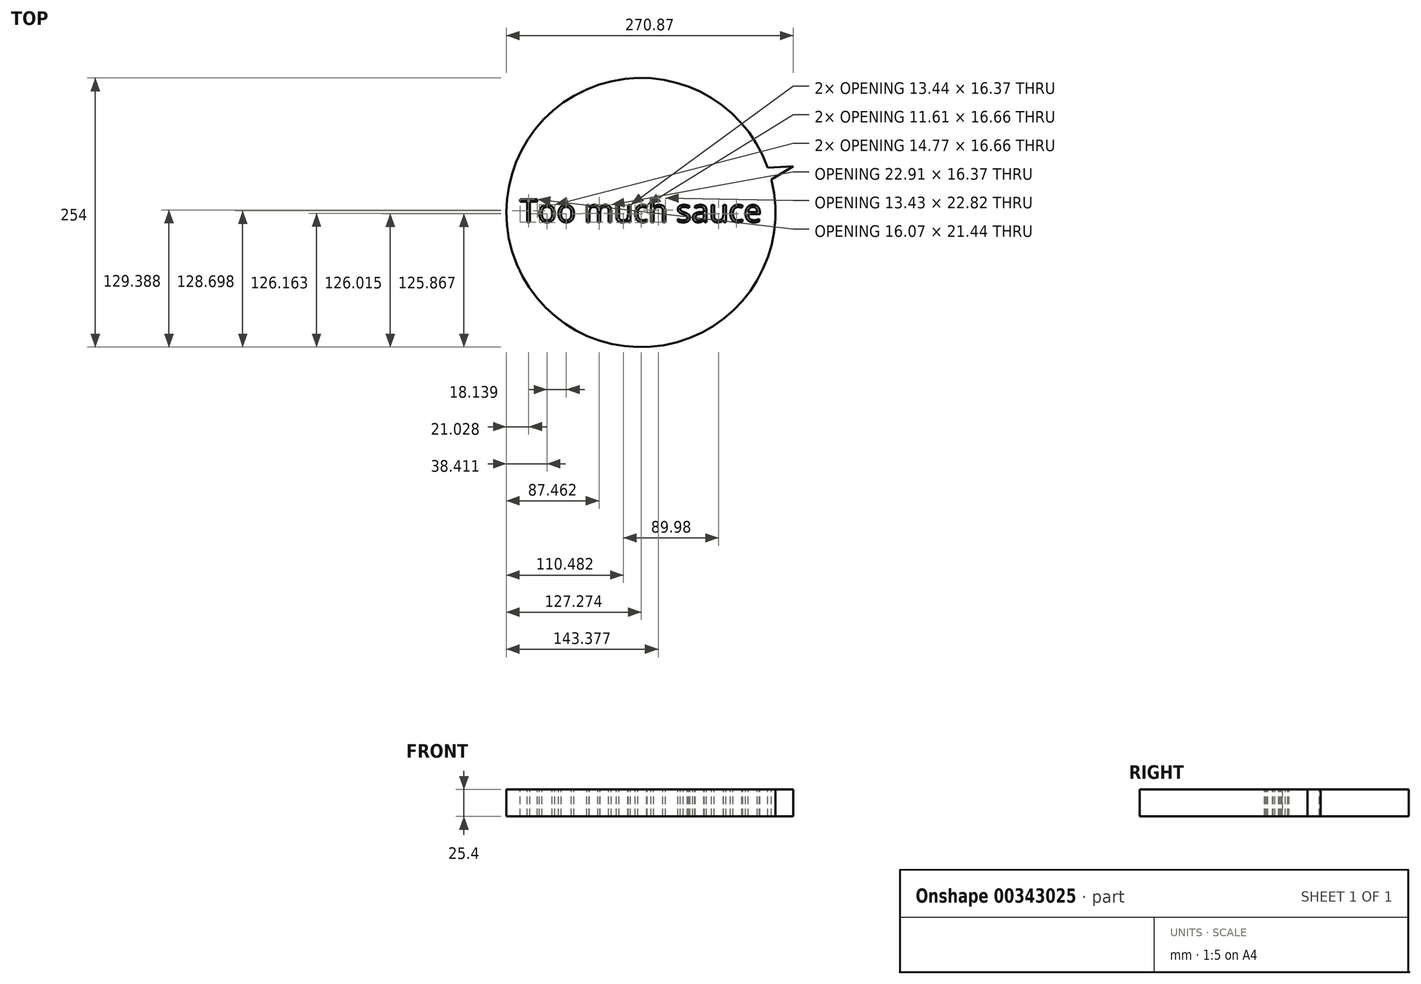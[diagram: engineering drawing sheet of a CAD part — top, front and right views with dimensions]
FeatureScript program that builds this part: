
annotation { "Feature Type Name" : "Feature", "Feature Type Description" : "" }
export const myFeature = defineFeature(function(context is Context, id is Id, definition is map)
    precondition{}
    {
        {
            var Q0;
            Q0=qCreatedBy(makeId("Top.planeOp"),FACE);
            var sketch = newSketch(context, id + "F0", { "sketchPlane" : qUnion([Q0])});
            skCircle(sketch, "E0", {"center": v(0, 0) * mm, "radius": 127 * mm});
            skSolve(sketch);
        }
        {
            var Q0;
            Q0 = qSketchRegion(id + "F0", true);
            extrude(context, id + "F1", {"entities" : qUnion([Q0]), "endBound" : BoundingType.SYMMETRIC, "depth" : 25.4 * mm});
        }
        {
            var Q0;
            Q0=makeQuery(id+"F1.opExtrude","CAP_FACE",FACE,{"disambiguationData":[OSD([sQuery(id+"F0.wireOp",EDGE,"E0")])],"isStart":false});
            var sketch = newSketch(context, id + "F2", { "sketchPlane" : qUnion([Q0])});
            skLineSegment(sketch, "E1", {"start": v(0, 0) * mm, "end": v(123.1, 31.24) * mm, "construction": true});
            skLineSegment(sketch, "E2", {"start": v(0, 0) * mm, "end": v(119.75, 42.3) * mm, "construction": true});
            skLineSegment(sketch, "E3", {"start": v(119.75, 42.3) * mm, "end": v(123.1, 31.24) * mm});
            skLineSegment(sketch, "E4", {"start": v(119.75, 42.3) * mm, "end": v(143.87, 43.57) * mm});
            skLineSegment(sketch, "E5", {"start": v(143.87, 43.57) * mm, "end": v(123.1, 31.24) * mm});
            skSolve(sketch);
        }
        {
            var Q0;
            Q0 = qSketchRegion(id + "F2", true);
            extrude(context, id + "F3", {"entities" : qUnion([Q0]), "operationType" : NewBodyOperationType.ADD, "oppositeDirection" : true, "depth" : 25.4 * mm});
        }
        {
            var Q0;
            {var subQ0=sQuery(id+"F2.wireOp",EDGE,"E5");var subQ1=sQuery(id+"F2.wireOp",EDGE,"E4");var subQ2=sQuery(id+"F2.wireOp",EDGE,"E3");Q0=makeQuery(id+"FsgY7ZD5xx5v8C2_1.68.F3.boolean.opBoolean","MERGE",FACE,{"derivedFrom":[makeQuery(id+"FsgY7ZD5xx5v8C2_1.67.F3.boolean.opBoolean","MERGE",FACE,{"derivedFrom":[makeQuery(id+"FsgY7ZD5xx5v8C2_1.66.F3.boolean.opBoolean","MERGE",FACE,{"derivedFrom":[makeQuery(id+"FsgY7ZD5xx5v8C2_1.65.F3.boolean.opBoolean","MERGE",FACE,{"derivedFrom":[makeQuery(id+"FsgY7ZD5xx5v8C2_1.64.F3.boolean.opBoolean","MERGE",FACE,{"derivedFrom":[makeQuery(id+"FsgY7ZD5xx5v8C2_1.63.F3.boolean.opBoolean","MERGE",FACE,{"derivedFrom":[makeQuery(id+"FsgY7ZD5xx5v8C2_1.62.F3.boolean.opBoolean","MERGE",FACE,{"derivedFrom":[makeQuery(id+"FsgY7ZD5xx5v8C2_1.61.F3.boolean.opBoolean","MERGE",FACE,{"derivedFrom":[makeQuery(id+"FsgY7ZD5xx5v8C2_1.60.F3.boolean.opBoolean","MERGE",FACE,{"derivedFrom":[makeQuery(id+"FsgY7ZD5xx5v8C2_1.59.F3.boolean.opBoolean","MERGE",FACE,{"derivedFrom":[makeQuery(id+"FsgY7ZD5xx5v8C2_1.58.F3.boolean.opBoolean","MERGE",FACE,{"derivedFrom":[makeQuery(id+"FsgY7ZD5xx5v8C2_1.57.F3.boolean.opBoolean","MERGE",FACE,{"derivedFrom":[makeQuery(id+"FsgY7ZD5xx5v8C2_1.56.F3.boolean.opBoolean","MERGE",FACE,{"derivedFrom":[makeQuery(id+"FsgY7ZD5xx5v8C2_1.55.F3.boolean.opBoolean","MERGE",FACE,{"derivedFrom":[makeQuery(id+"FsgY7ZD5xx5v8C2_1.54.F3.boolean.opBoolean","MERGE",FACE,{"derivedFrom":[makeQuery(id+"FsgY7ZD5xx5v8C2_1.53.F3.boolean.opBoolean","MERGE",FACE,{"derivedFrom":[makeQuery(id+"FsgY7ZD5xx5v8C2_1.52.F3.boolean.opBoolean","MERGE",FACE,{"derivedFrom":[makeQuery(id+"FsgY7ZD5xx5v8C2_1.51.F3.boolean.opBoolean","MERGE",FACE,{"derivedFrom":[makeQuery(id+"FsgY7ZD5xx5v8C2_1.50.F3.boolean.opBoolean","MERGE",FACE,{"derivedFrom":[makeQuery(id+"FsgY7ZD5xx5v8C2_1.49.F3.boolean.opBoolean","MERGE",FACE,{"derivedFrom":[makeQuery(id+"FsgY7ZD5xx5v8C2_1.48.F3.boolean.opBoolean","MERGE",FACE,{"derivedFrom":[makeQuery(id+"FsgY7ZD5xx5v8C2_1.47.F3.boolean.opBoolean","MERGE",FACE,{"derivedFrom":[makeQuery(id+"FsgY7ZD5xx5v8C2_1.46.F3.boolean.opBoolean","MERGE",FACE,{"derivedFrom":[makeQuery(id+"FsgY7ZD5xx5v8C2_1.45.F3.boolean.opBoolean","MERGE",FACE,{"derivedFrom":[makeQuery(id+"FsgY7ZD5xx5v8C2_1.44.F3.boolean.opBoolean","MERGE",FACE,{"derivedFrom":[makeQuery(id+"FsgY7ZD5xx5v8C2_1.43.F3.boolean.opBoolean","MERGE",FACE,{"derivedFrom":[makeQuery(id+"FsgY7ZD5xx5v8C2_1.42.F3.boolean.opBoolean","MERGE",FACE,{"derivedFrom":[makeQuery(id+"FsgY7ZD5xx5v8C2_1.41.F3.boolean.opBoolean","MERGE",FACE,{"derivedFrom":[makeQuery(id+"FsgY7ZD5xx5v8C2_1.40.F3.boolean.opBoolean","MERGE",FACE,{"derivedFrom":[makeQuery(id+"FsgY7ZD5xx5v8C2_1.39.F3.boolean.opBoolean","MERGE",FACE,{"derivedFrom":[makeQuery(id+"FsgY7ZD5xx5v8C2_1.38.F3.boolean.opBoolean","MERGE",FACE,{"derivedFrom":[makeQuery(id+"FsgY7ZD5xx5v8C2_1.37.F3.boolean.opBoolean","MERGE",FACE,{"derivedFrom":[makeQuery(id+"FsgY7ZD5xx5v8C2_1.36.F3.boolean.opBoolean","MERGE",FACE,{"derivedFrom":[makeQuery(id+"FsgY7ZD5xx5v8C2_1.35.F3.boolean.opBoolean","MERGE",FACE,{"derivedFrom":[makeQuery(id+"FsgY7ZD5xx5v8C2_1.34.F3.boolean.opBoolean","MERGE",FACE,{"derivedFrom":[makeQuery(id+"FsgY7ZD5xx5v8C2_1.33.F3.boolean.opBoolean","MERGE",FACE,{"derivedFrom":[makeQuery(id+"FsgY7ZD5xx5v8C2_1.32.F3.boolean.opBoolean","MERGE",FACE,{"derivedFrom":[makeQuery(id+"FsgY7ZD5xx5v8C2_1.31.F3.boolean.opBoolean","MERGE",FACE,{"derivedFrom":[makeQuery(id+"FsgY7ZD5xx5v8C2_1.30.F3.boolean.opBoolean","MERGE",FACE,{"derivedFrom":[makeQuery(id+"FsgY7ZD5xx5v8C2_1.29.F3.boolean.opBoolean","MERGE",FACE,{"derivedFrom":[makeQuery(id+"FsgY7ZD5xx5v8C2_1.28.F3.boolean.opBoolean","MERGE",FACE,{"derivedFrom":[makeQuery(id+"FsgY7ZD5xx5v8C2_1.27.F3.boolean.opBoolean","MERGE",FACE,{"derivedFrom":[makeQuery(id+"FsgY7ZD5xx5v8C2_1.26.F3.boolean.opBoolean","MERGE",FACE,{"derivedFrom":[makeQuery(id+"FsgY7ZD5xx5v8C2_1.25.F3.boolean.opBoolean","MERGE",FACE,{"derivedFrom":[makeQuery(id+"FsgY7ZD5xx5v8C2_1.24.F3.boolean.opBoolean","MERGE",FACE,{"derivedFrom":[makeQuery(id+"FsgY7ZD5xx5v8C2_1.23.F3.boolean.opBoolean","MERGE",FACE,{"derivedFrom":[makeQuery(id+"FsgY7ZD5xx5v8C2_1.22.F3.boolean.opBoolean","MERGE",FACE,{"derivedFrom":[makeQuery(id+"FsgY7ZD5xx5v8C2_1.21.F3.boolean.opBoolean","MERGE",FACE,{"derivedFrom":[makeQuery(id+"FsgY7ZD5xx5v8C2_1.20.F3.boolean.opBoolean","MERGE",FACE,{"derivedFrom":[makeQuery(id+"FsgY7ZD5xx5v8C2_1.19.F3.boolean.opBoolean","MERGE",FACE,{"derivedFrom":[makeQuery(id+"FsgY7ZD5xx5v8C2_1.18.F3.boolean.opBoolean","MERGE",FACE,{"derivedFrom":[makeQuery(id+"FsgY7ZD5xx5v8C2_1.17.F3.boolean.opBoolean","MERGE",FACE,{"derivedFrom":[makeQuery(id+"FsgY7ZD5xx5v8C2_1.16.F3.boolean.opBoolean","MERGE",FACE,{"derivedFrom":[makeQuery(id+"FsgY7ZD5xx5v8C2_1.15.F3.boolean.opBoolean","MERGE",FACE,{"derivedFrom":[makeQuery(id+"FsgY7ZD5xx5v8C2_1.14.F3.boolean.opBoolean","MERGE",FACE,{"derivedFrom":[makeQuery(id+"FsgY7ZD5xx5v8C2_1.13.F3.boolean.opBoolean","MERGE",FACE,{"derivedFrom":[makeQuery(id+"FsgY7ZD5xx5v8C2_1.12.F3.boolean.opBoolean","MERGE",FACE,{"derivedFrom":[makeQuery(id+"FsgY7ZD5xx5v8C2_1.11.F3.boolean.opBoolean","MERGE",FACE,{"derivedFrom":[makeQuery(id+"FsgY7ZD5xx5v8C2_1.10.F3.boolean.opBoolean","MERGE",FACE,{"derivedFrom":[makeQuery(id+"FsgY7ZD5xx5v8C2_1.9.F3.boolean.opBoolean","MERGE",FACE,{"derivedFrom":[makeQuery(id+"FsgY7ZD5xx5v8C2_1.8.F3.boolean.opBoolean","MERGE",FACE,{"derivedFrom":[makeQuery(id+"FsgY7ZD5xx5v8C2_1.7.F3.boolean.opBoolean","MERGE",FACE,{"derivedFrom":[makeQuery(id+"FsgY7ZD5xx5v8C2_1.6.F3.boolean.opBoolean","MERGE",FACE,{"derivedFrom":[makeQuery(id+"FsgY7ZD5xx5v8C2_1.5.F3.boolean.opBoolean","MERGE",FACE,{"derivedFrom":[makeQuery(id+"FsgY7ZD5xx5v8C2_1.4.F3.boolean.opBoolean","MERGE",FACE,{"derivedFrom":[makeQuery(id+"FsgY7ZD5xx5v8C2_1.3.F3.boolean.opBoolean","MERGE",FACE,{"derivedFrom":[makeQuery(id+"FsgY7ZD5xx5v8C2_1.2.F3.boolean.opBoolean","MERGE",FACE,{"derivedFrom":[makeQuery(id+"FsgY7ZD5xx5v8C2_1.1.F3.boolean.opBoolean","MERGE",FACE,{"derivedFrom":[makeQuery(id+"F3.boolean.opBoolean","MERGE",FACE,{"derivedFrom":[makeQuery(id+"F1.opExtrude","CAP_FACE",FACE,{"disambiguationData":[OSD([sQuery(id+"F0.wireOp",EDGE,"E0")])],"isStart":false}),makeQuery(id+"F3.opExtrude","CAP_FACE",FACE,{"disambiguationData":[OSD([subQ2,subQ1,subQ0])],"isStart":true})]}),makeQuery(id+"FsgY7ZD5xx5v8C2_1.1.F3.opExtrude","CAP_FACE",FACE,{"disambiguationData":[OSD([subQ2,subQ1,subQ0])],"isStart":true})]}),makeQuery(id+"FsgY7ZD5xx5v8C2_1.2.F3.opExtrude","CAP_FACE",FACE,{"disambiguationData":[OSD([subQ2,subQ1,subQ0])],"isStart":true})]}),makeQuery(id+"FsgY7ZD5xx5v8C2_1.3.F3.opExtrude","CAP_FACE",FACE,{"disambiguationData":[OSD([subQ2,subQ1,subQ0])],"isStart":true})]}),makeQuery(id+"FsgY7ZD5xx5v8C2_1.4.F3.opExtrude","CAP_FACE",FACE,{"disambiguationData":[OSD([subQ2,subQ1,subQ0])],"isStart":true})]}),makeQuery(id+"FsgY7ZD5xx5v8C2_1.5.F3.opExtrude","CAP_FACE",FACE,{"disambiguationData":[OSD([subQ2,subQ1,subQ0])],"isStart":true})]}),makeQuery(id+"FsgY7ZD5xx5v8C2_1.6.F3.opExtrude","CAP_FACE",FACE,{"disambiguationData":[OSD([subQ2,subQ1,subQ0])],"isStart":true})]}),makeQuery(id+"FsgY7ZD5xx5v8C2_1.7.F3.opExtrude","CAP_FACE",FACE,{"disambiguationData":[OSD([subQ2,subQ1,subQ0])],"isStart":true})]}),makeQuery(id+"FsgY7ZD5xx5v8C2_1.8.F3.opExtrude","CAP_FACE",FACE,{"disambiguationData":[OSD([subQ2,subQ1,subQ0])],"isStart":true})]}),makeQuery(id+"FsgY7ZD5xx5v8C2_1.9.F3.opExtrude","CAP_FACE",FACE,{"disambiguationData":[OSD([subQ2,subQ1,subQ0])],"isStart":true})]}),makeQuery(id+"FsgY7ZD5xx5v8C2_1.10.F3.opExtrude","CAP_FACE",FACE,{"disambiguationData":[OSD([subQ2,subQ1,subQ0])],"isStart":true})]}),makeQuery(id+"FsgY7ZD5xx5v8C2_1.11.F3.opExtrude","CAP_FACE",FACE,{"disambiguationData":[OSD([subQ2,subQ1,subQ0])],"isStart":true})]}),makeQuery(id+"FsgY7ZD5xx5v8C2_1.12.F3.opExtrude","CAP_FACE",FACE,{"disambiguationData":[OSD([subQ2,subQ1,subQ0])],"isStart":true})]}),makeQuery(id+"FsgY7ZD5xx5v8C2_1.13.F3.opExtrude","CAP_FACE",FACE,{"disambiguationData":[OSD([subQ2,subQ1,subQ0])],"isStart":true})]}),makeQuery(id+"FsgY7ZD5xx5v8C2_1.14.F3.opExtrude","CAP_FACE",FACE,{"disambiguationData":[OSD([subQ2,subQ1,subQ0])],"isStart":true})]}),makeQuery(id+"FsgY7ZD5xx5v8C2_1.15.F3.opExtrude","CAP_FACE",FACE,{"disambiguationData":[OSD([subQ2,subQ1,subQ0])],"isStart":true})]}),makeQuery(id+"FsgY7ZD5xx5v8C2_1.16.F3.opExtrude","CAP_FACE",FACE,{"disambiguationData":[OSD([subQ2,subQ1,subQ0])],"isStart":true})]}),makeQuery(id+"FsgY7ZD5xx5v8C2_1.17.F3.opExtrude","CAP_FACE",FACE,{"disambiguationData":[OSD([subQ2,subQ1,subQ0])],"isStart":true})]}),makeQuery(id+"FsgY7ZD5xx5v8C2_1.18.F3.opExtrude","CAP_FACE",FACE,{"disambiguationData":[OSD([subQ2,subQ1,subQ0])],"isStart":true})]}),makeQuery(id+"FsgY7ZD5xx5v8C2_1.19.F3.opExtrude","CAP_FACE",FACE,{"disambiguationData":[OSD([subQ2,subQ1,subQ0])],"isStart":true})]}),makeQuery(id+"FsgY7ZD5xx5v8C2_1.20.F3.opExtrude","CAP_FACE",FACE,{"disambiguationData":[OSD([subQ2,subQ1,subQ0])],"isStart":true})]}),makeQuery(id+"FsgY7ZD5xx5v8C2_1.21.F3.opExtrude","CAP_FACE",FACE,{"disambiguationData":[OSD([subQ2,subQ1,subQ0])],"isStart":true})]}),makeQuery(id+"FsgY7ZD5xx5v8C2_1.22.F3.opExtrude","CAP_FACE",FACE,{"disambiguationData":[OSD([subQ2,subQ1,subQ0])],"isStart":true})]}),makeQuery(id+"FsgY7ZD5xx5v8C2_1.23.F3.opExtrude","CAP_FACE",FACE,{"disambiguationData":[OSD([subQ2,subQ1,subQ0])],"isStart":true})]}),makeQuery(id+"FsgY7ZD5xx5v8C2_1.24.F3.opExtrude","CAP_FACE",FACE,{"disambiguationData":[OSD([subQ2,subQ1,subQ0])],"isStart":true})]}),makeQuery(id+"FsgY7ZD5xx5v8C2_1.25.F3.opExtrude","CAP_FACE",FACE,{"disambiguationData":[OSD([subQ2,subQ1,subQ0])],"isStart":true})]}),makeQuery(id+"FsgY7ZD5xx5v8C2_1.26.F3.opExtrude","CAP_FACE",FACE,{"disambiguationData":[OSD([subQ2,subQ1,subQ0])],"isStart":true})]}),makeQuery(id+"FsgY7ZD5xx5v8C2_1.27.F3.opExtrude","CAP_FACE",FACE,{"disambiguationData":[OSD([subQ2,subQ1,subQ0])],"isStart":true})]}),makeQuery(id+"FsgY7ZD5xx5v8C2_1.28.F3.opExtrude","CAP_FACE",FACE,{"disambiguationData":[OSD([subQ2,subQ1,subQ0])],"isStart":true})]}),makeQuery(id+"FsgY7ZD5xx5v8C2_1.29.F3.opExtrude","CAP_FACE",FACE,{"disambiguationData":[OSD([subQ2,subQ1,subQ0])],"isStart":true})]}),makeQuery(id+"FsgY7ZD5xx5v8C2_1.30.F3.opExtrude","CAP_FACE",FACE,{"disambiguationData":[OSD([subQ2,subQ1,subQ0])],"isStart":true})]}),makeQuery(id+"FsgY7ZD5xx5v8C2_1.31.F3.opExtrude","CAP_FACE",FACE,{"disambiguationData":[OSD([subQ2,subQ1,subQ0])],"isStart":true})]}),makeQuery(id+"FsgY7ZD5xx5v8C2_1.32.F3.opExtrude","CAP_FACE",FACE,{"disambiguationData":[OSD([subQ2,subQ1,subQ0])],"isStart":true})]}),makeQuery(id+"FsgY7ZD5xx5v8C2_1.33.F3.opExtrude","CAP_FACE",FACE,{"disambiguationData":[OSD([subQ2,subQ1,subQ0])],"isStart":true})]}),makeQuery(id+"FsgY7ZD5xx5v8C2_1.34.F3.opExtrude","CAP_FACE",FACE,{"disambiguationData":[OSD([subQ2,subQ1,subQ0])],"isStart":true})]}),makeQuery(id+"FsgY7ZD5xx5v8C2_1.35.F3.opExtrude","CAP_FACE",FACE,{"disambiguationData":[OSD([subQ2,subQ1,subQ0])],"isStart":true})]}),makeQuery(id+"FsgY7ZD5xx5v8C2_1.36.F3.opExtrude","CAP_FACE",FACE,{"disambiguationData":[OSD([subQ2,subQ1,subQ0])],"isStart":true})]}),makeQuery(id+"FsgY7ZD5xx5v8C2_1.37.F3.opExtrude","CAP_FACE",FACE,{"disambiguationData":[OSD([subQ2,subQ1,subQ0])],"isStart":true})]}),makeQuery(id+"FsgY7ZD5xx5v8C2_1.38.F3.opExtrude","CAP_FACE",FACE,{"disambiguationData":[OSD([subQ2,subQ1,subQ0])],"isStart":true})]}),makeQuery(id+"FsgY7ZD5xx5v8C2_1.39.F3.opExtrude","CAP_FACE",FACE,{"disambiguationData":[OSD([subQ2,subQ1,subQ0])],"isStart":true})]}),makeQuery(id+"FsgY7ZD5xx5v8C2_1.40.F3.opExtrude","CAP_FACE",FACE,{"disambiguationData":[OSD([subQ2,subQ1,subQ0])],"isStart":true})]}),makeQuery(id+"FsgY7ZD5xx5v8C2_1.41.F3.opExtrude","CAP_FACE",FACE,{"disambiguationData":[OSD([subQ2,subQ1,subQ0])],"isStart":true})]}),makeQuery(id+"FsgY7ZD5xx5v8C2_1.42.F3.opExtrude","CAP_FACE",FACE,{"disambiguationData":[OSD([subQ2,subQ1,subQ0])],"isStart":true})]}),makeQuery(id+"FsgY7ZD5xx5v8C2_1.43.F3.opExtrude","CAP_FACE",FACE,{"disambiguationData":[OSD([subQ2,subQ1,subQ0])],"isStart":true})]}),makeQuery(id+"FsgY7ZD5xx5v8C2_1.44.F3.opExtrude","CAP_FACE",FACE,{"disambiguationData":[OSD([subQ2,subQ1,subQ0])],"isStart":true})]}),makeQuery(id+"FsgY7ZD5xx5v8C2_1.45.F3.opExtrude","CAP_FACE",FACE,{"disambiguationData":[OSD([subQ2,subQ1,subQ0])],"isStart":true})]}),makeQuery(id+"FsgY7ZD5xx5v8C2_1.46.F3.opExtrude","CAP_FACE",FACE,{"disambiguationData":[OSD([subQ2,subQ1,subQ0])],"isStart":true})]}),makeQuery(id+"FsgY7ZD5xx5v8C2_1.47.F3.opExtrude","CAP_FACE",FACE,{"disambiguationData":[OSD([subQ2,subQ1,subQ0])],"isStart":true})]}),makeQuery(id+"FsgY7ZD5xx5v8C2_1.48.F3.opExtrude","CAP_FACE",FACE,{"disambiguationData":[OSD([subQ2,subQ1,subQ0])],"isStart":true})]}),makeQuery(id+"FsgY7ZD5xx5v8C2_1.49.F3.opExtrude","CAP_FACE",FACE,{"disambiguationData":[OSD([subQ2,subQ1,subQ0])],"isStart":true})]}),makeQuery(id+"FsgY7ZD5xx5v8C2_1.50.F3.opExtrude","CAP_FACE",FACE,{"disambiguationData":[OSD([subQ2,subQ1,subQ0])],"isStart":true})]}),makeQuery(id+"FsgY7ZD5xx5v8C2_1.51.F3.opExtrude","CAP_FACE",FACE,{"disambiguationData":[OSD([subQ2,subQ1,subQ0])],"isStart":true})]}),makeQuery(id+"FsgY7ZD5xx5v8C2_1.52.F3.opExtrude","CAP_FACE",FACE,{"disambiguationData":[OSD([subQ2,subQ1,subQ0])],"isStart":true})]}),makeQuery(id+"FsgY7ZD5xx5v8C2_1.53.F3.opExtrude","CAP_FACE",FACE,{"disambiguationData":[OSD([subQ2,subQ1,subQ0])],"isStart":true})]}),makeQuery(id+"FsgY7ZD5xx5v8C2_1.54.F3.opExtrude","CAP_FACE",FACE,{"disambiguationData":[OSD([subQ2,subQ1,subQ0])],"isStart":true})]}),makeQuery(id+"FsgY7ZD5xx5v8C2_1.55.F3.opExtrude","CAP_FACE",FACE,{"disambiguationData":[OSD([subQ2,subQ1,subQ0])],"isStart":true})]}),makeQuery(id+"FsgY7ZD5xx5v8C2_1.56.F3.opExtrude","CAP_FACE",FACE,{"disambiguationData":[OSD([subQ2,subQ1,subQ0])],"isStart":true})]}),makeQuery(id+"FsgY7ZD5xx5v8C2_1.57.F3.opExtrude","CAP_FACE",FACE,{"disambiguationData":[OSD([subQ2,subQ1,subQ0])],"isStart":true})]}),makeQuery(id+"FsgY7ZD5xx5v8C2_1.58.F3.opExtrude","CAP_FACE",FACE,{"disambiguationData":[OSD([subQ2,subQ1,subQ0])],"isStart":true})]}),makeQuery(id+"FsgY7ZD5xx5v8C2_1.59.F3.opExtrude","CAP_FACE",FACE,{"disambiguationData":[OSD([subQ2,subQ1,subQ0])],"isStart":true})]}),makeQuery(id+"FsgY7ZD5xx5v8C2_1.60.F3.opExtrude","CAP_FACE",FACE,{"disambiguationData":[OSD([subQ2,subQ1,subQ0])],"isStart":true})]}),makeQuery(id+"FsgY7ZD5xx5v8C2_1.61.F3.opExtrude","CAP_FACE",FACE,{"disambiguationData":[OSD([subQ2,subQ1,subQ0])],"isStart":true})]}),makeQuery(id+"FsgY7ZD5xx5v8C2_1.62.F3.opExtrude","CAP_FACE",FACE,{"disambiguationData":[OSD([subQ2,subQ1,subQ0])],"isStart":true})]}),makeQuery(id+"FsgY7ZD5xx5v8C2_1.63.F3.opExtrude","CAP_FACE",FACE,{"disambiguationData":[OSD([subQ2,subQ1,subQ0])],"isStart":true})]}),makeQuery(id+"FsgY7ZD5xx5v8C2_1.64.F3.opExtrude","CAP_FACE",FACE,{"disambiguationData":[OSD([subQ2,subQ1,subQ0])],"isStart":true})]}),makeQuery(id+"FsgY7ZD5xx5v8C2_1.65.F3.opExtrude","CAP_FACE",FACE,{"disambiguationData":[OSD([subQ2,subQ1,subQ0])],"isStart":true})]}),makeQuery(id+"FsgY7ZD5xx5v8C2_1.66.F3.opExtrude","CAP_FACE",FACE,{"disambiguationData":[OSD([subQ2,subQ1,subQ0])],"isStart":true})]}),makeQuery(id+"FsgY7ZD5xx5v8C2_1.67.F3.opExtrude","CAP_FACE",FACE,{"disambiguationData":[OSD([subQ2,subQ1,subQ0])],"isStart":true})]}),makeQuery(id+"FsgY7ZD5xx5v8C2_1.68.F3.opExtrude","CAP_FACE",FACE,{"disambiguationData":[OSD([subQ2,subQ1,subQ0])],"isStart":true})]});}
            var sketch = newSketch(context, id + "F4", { "sketchPlane" : qUnion([Q0])});
            skText(sketch, "E6", { "text": "Too much sauce ", "fontName": "OpenSans-Regular.ttf"});
            const initialGuessF4  = {"E6": [-0.11427, -0.00902, 1, 0, 0.02162]};
            skSetInitialGuess(sketch, initialGuessF4);
            skSolve(sketch);
        }
        {
            var Q0;
            Q0 = qSketchRegion(id + "F4", true);
            extrude(context, id + "F5", {"entities" : qUnion([Q0]), "operationType" : NewBodyOperationType.REMOVE, "endBound" : BoundingType.THROUGH_ALL, "oppositeDirection" : true, "depth" : 25.4 * mm});
        }
    });
